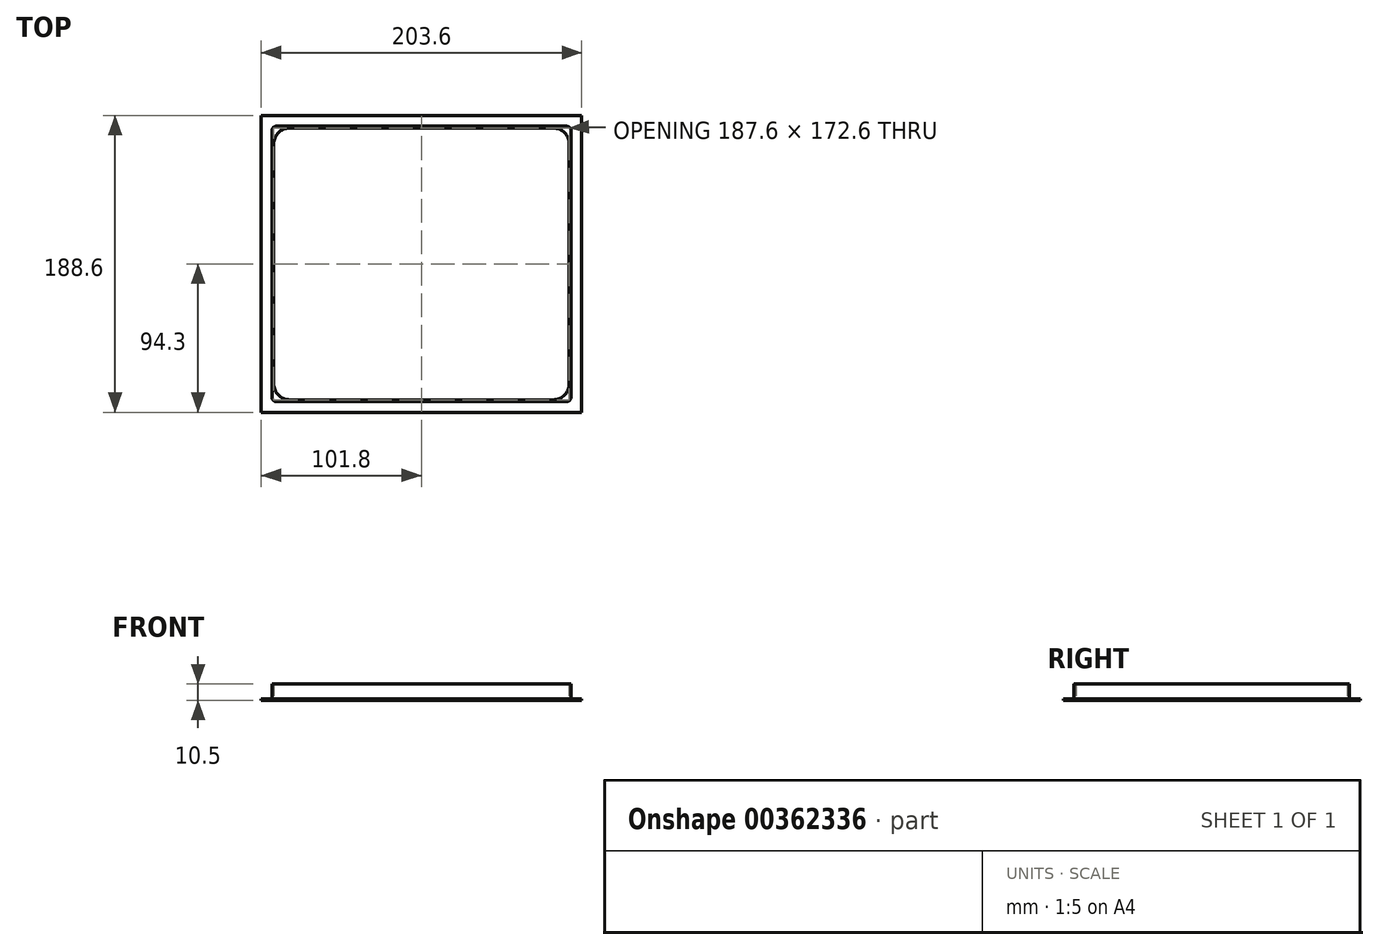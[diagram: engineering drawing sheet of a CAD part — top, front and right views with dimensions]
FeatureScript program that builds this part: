
annotation { "Feature Type Name" : "Feature", "Feature Type Description" : "" }
export const myFeature = defineFeature(function(context is Context, id is Id, definition is map)
    precondition{}
    {
        {
            var Q0;
            Q0=qCreatedBy(makeId("Top.planeOp"),FACE);
            var sketch = newSketch(context, id + "F0", { "sketchPlane" : qUnion([Q0])});
            skLineSegment(sketch, "E0.bottom", {"start": v(92, -87.5) * mm, "end": v(-92, -87.5) * mm});
            skLineSegment(sketch, "E0.top", {"start": v(92, 87.5) * mm, "end": v(-92, 87.5) * mm});
            skLineSegment(sketch, "E0.left", {"start": v(95, -84.5) * mm, "end": v(95, 84.5) * mm});
            skLineSegment(sketch, "E0.right", {"start": v(-95, -84.5) * mm, "end": v(-95, 84.5) * mm});
            skPoint(sketch, "E0.middle", {"position": v(0, 0) * mm});
            skLineSegment(sketch, "E1.bottom", {"start": v(83.8, -86.3) * mm, "end": v(-83.8, -86.3) * mm});
            skLineSegment(sketch, "E1.top", {"start": v(83.8, 86.3) * mm, "end": v(-83.8, 86.3) * mm});
            skLineSegment(sketch, "E1.left", {"start": v(93.8, -76.3) * mm, "end": v(93.8, 76.3) * mm});
            skLineSegment(sketch, "E1.right", {"start": v(-93.8, -76.3) * mm, "end": v(-93.8, 76.3) * mm});
            skPoint(sketch, "E2.visualSharp", {"position": v(-93.8, 86.3) * mm});
            skArc(sketch, "E2.filletArc", {"start": v(-83.8, 86.3) * mm, "mid": v(-90.87, 83.37) * mm, "end": v(-93.8, 76.3) * mm});
            skPoint(sketch, "E3.visualSharp", {"position": v(93.8, 86.3) * mm});
            skArc(sketch, "E3.filletArc", {"start": v(93.8, 76.3) * mm, "mid": v(90.87, 83.37) * mm, "end": v(83.8, 86.3) * mm});
            skPoint(sketch, "E4.visualSharp", {"position": v(93.8, -86.3) * mm});
            skArc(sketch, "E4.filletArc", {"start": v(83.8, -86.3) * mm, "mid": v(90.87, -83.37) * mm, "end": v(93.8, -76.3) * mm});
            skPoint(sketch, "E5.visualSharp", {"position": v(-93.8, -86.3) * mm});
            skArc(sketch, "E5.filletArc", {"start": v(-93.8, -76.3) * mm, "mid": v(-90.87, -83.37) * mm, "end": v(-83.8, -86.3) * mm});
            skPoint(sketch, "E6.visualSharp", {"position": v(95, 87.5) * mm});
            skArc(sketch, "E6.filletArc", {"start": v(95, 84.5) * mm, "mid": v(94.12, 86.62) * mm, "end": v(92, 87.5) * mm});
            skPoint(sketch, "E7.visualSharp", {"position": v(-95, 87.5) * mm});
            skArc(sketch, "E7.filletArc", {"start": v(-92, 87.5) * mm, "mid": v(-94.12, 86.62) * mm, "end": v(-95, 84.5) * mm});
            skPoint(sketch, "E8.visualSharp", {"position": v(-95, -87.5) * mm});
            skArc(sketch, "E8.filletArc", {"start": v(-95, -84.5) * mm, "mid": v(-94.12, -86.62) * mm, "end": v(-92, -87.5) * mm});
            skPoint(sketch, "E9.visualSharp", {"position": v(95, -87.5) * mm});
            skArc(sketch, "E9.filletArc", {"start": v(92, -87.5) * mm, "mid": v(94.12, -86.62) * mm, "end": v(95, -84.5) * mm});
            skLineSegment(sketch, "E10.bottom", {"start": v(101.8, -94.3) * mm, "end": v(-101.8, -94.3) * mm});
            skLineSegment(sketch, "E10.top", {"start": v(101.8, 94.3) * mm, "end": v(-101.8, 94.3) * mm});
            skLineSegment(sketch, "E10.left", {"start": v(101.8, -94.3) * mm, "end": v(101.8, 94.3) * mm});
            skLineSegment(sketch, "E10.right", {"start": v(-101.8, -94.3) * mm, "end": v(-101.8, 94.3) * mm});
            skSolve(sketch);
        }
        {
            var Q0;
            Q0=makeQuery(id+"F0.imprint","IMPRINT",FACE,{"disambiguationData":[TD([[makeQuery(id+"F0.imprint","IMPRINT",EDGE,{"derivedFrom":sQuery(id+"F0.wireOp",EDGE,"E0.bottom")}),-1.0]])]});
            extrude(context, id + "F1", {"entities" : qUnion([Q0]), "depth" : 9.5 * mm});
        }
        {
            var Q0;
            Q0=makeQuery(id+"F0.imprint","IMPRINT",FACE,{"disambiguationData":[TD([[makeQuery(id+"F0.imprint","IMPRINT",EDGE,{"derivedFrom":sQuery(id+"F0.wireOp",EDGE,"E0.bottom")}),1.0]])]});
            var Q1;
            Q1=makeQuery(id+"F0.imprint","IMPRINT",FACE,{"disambiguationData":[TD([[makeQuery(id+"F0.imprint","IMPRINT",EDGE,{"derivedFrom":sQuery(id+"F0.wireOp",EDGE,"E0.bottom")}),-1.0]])]});
            extrude(context, id + "F2", {"entities" : qUnion([Q0, Q1]), "operationType" : NewBodyOperationType.ADD, "oppositeDirection" : true, "depth" : 1 * mm});
        }
    });
